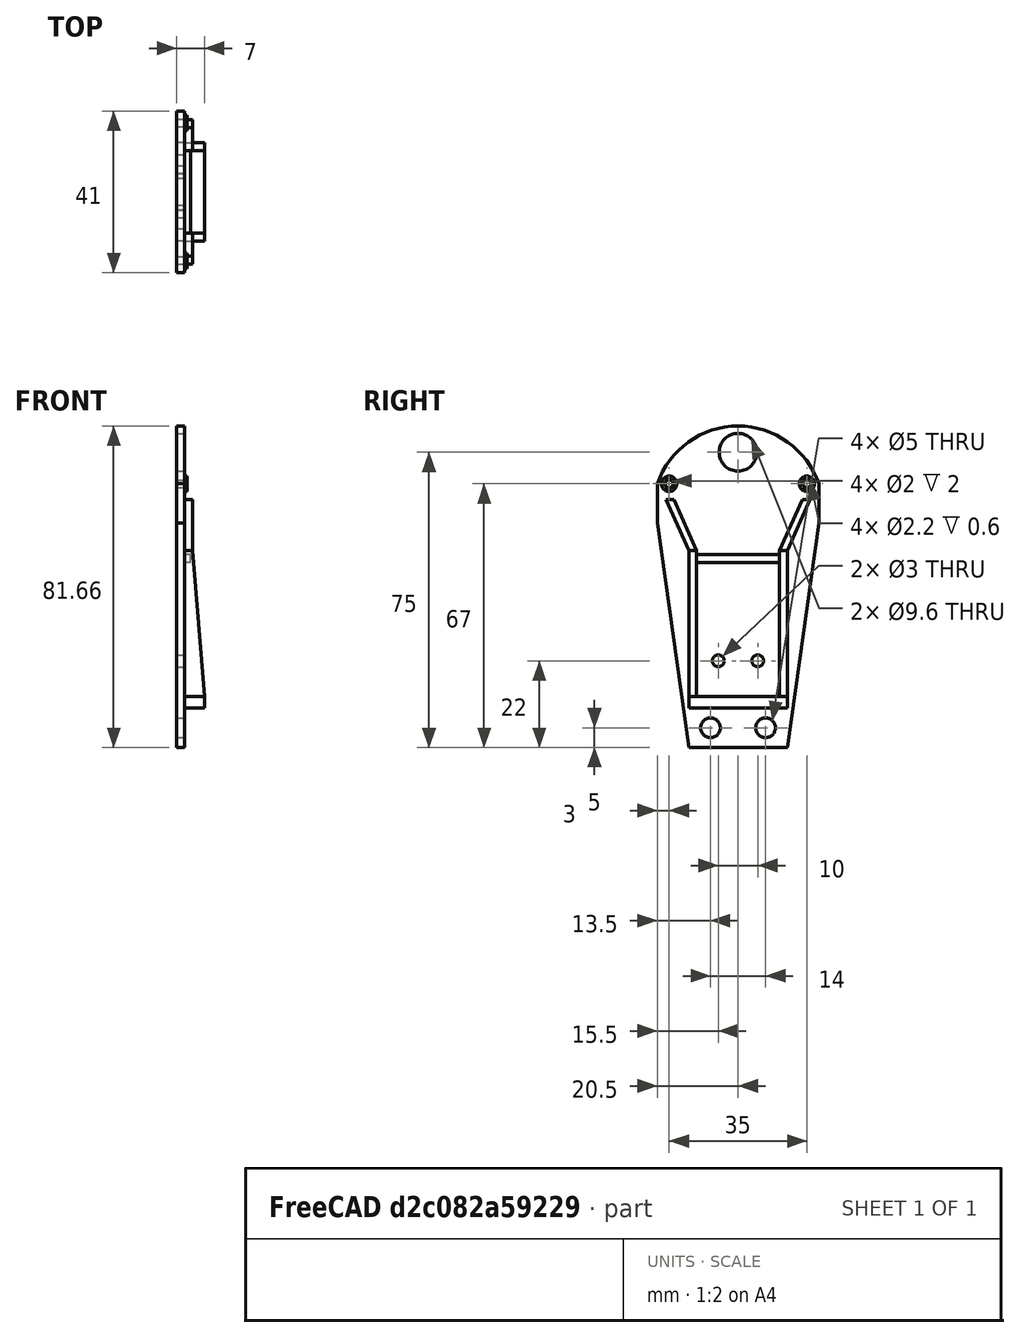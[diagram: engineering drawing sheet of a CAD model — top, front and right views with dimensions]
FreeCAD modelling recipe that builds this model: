
FCSTD DOCUMENT  (FreeCAD 0.16R4740 (Git))
Label: backplane
License: CC-BY 3.0
LicenseURL: http://creativecommons.org/licenses/by/3.0/
objects: Sketcher::SketchObject×6, Part::Fuse×6, PartDesign::Pad×5, Part::Mirroring×2, Part::MultiFuse×1, Part::Box×1, PartDesign::Pocket×1, Mesh::Feature×1
note: 28 computed .brp shape members not serialized (recipe doc carries the construction recipe); baked Part::Feature solids carry a one-line shape summary decoded from their .brp

FEATURE [Sketcher::SketchObject] Sketch001
  Placement = pos=(0,0,0) rot=(0.57735,-0.57735,-0.57735;2.0944rad)
  sketch-geometry (11):
    g0: Circle CenterX=0 CenterY=8 CenterZ=0 NormalX=0 NormalY=0 NormalZ=1 Radius=4.8
    g1: Circle CenterX=-17.5 CenterY=0 CenterZ=0 NormalX=0 NormalY=0 NormalZ=1 Radius=1
    g2: Circle CenterX=17.5 CenterY=0 CenterZ=0 NormalX=0 NormalY=0 NormalZ=1 Radius=1
    g3: ArcOfCircle CenterX=0 CenterY=-7 CenterZ=0 NormalX=0 NormalY=0 NormalZ=1 Radius=21.6622 StartAngle=0.32905 EndAngle=2.81254
    g4: LineSegment StartX=-20.5 StartY=0 StartZ=0 EndX=-20.5 EndY=-10 EndZ=0
    g5: LineSegment StartX=-20.5 StartY=-10 StartZ=0 EndX=-12.5 EndY=-67 EndZ=0
    g6: LineSegment StartX=-12.5 StartY=-67 StartZ=0 EndX=12.5 EndY=-67 EndZ=0
    g7: LineSegment StartX=12.5 StartY=-67 StartZ=0 EndX=20.5 EndY=-10 EndZ=0
    g8: LineSegment StartX=20.5 StartY=-10 StartZ=0 EndX=20.5 EndY=0 EndZ=0
    g9: Circle CenterX=-7 CenterY=-62 CenterZ=0 NormalX=0 NormalY=0 NormalZ=1 Radius=2.5
    g10: Circle CenterX=7 CenterY=-62 CenterZ=0 NormalX=0 NormalY=0 NormalZ=1 Radius=2.5
  constraints (34):
    c: Radius(g0) = 4.8
    c: DistanceY(g-1,g0) = 8
    c: DistanceX(g-1,g0) = 0
    c: DistanceX(g2,g1) = -35
    c: Radius(g1) = 1
    c: Radius(g2) = 1
    c: DistanceX(g-1,g1) = -17.5
    c: DistanceY(g1,g2) = 0
    c: DistanceY(g-1,g1) = 0
    c: DistanceX(g-1,g3) = 0
    c: DistanceY(g3,g3) = 0
    c: Coincident(g4,g5)
    c: Coincident(g5,g6)
    c: Horizontal(g6)
    c: Coincident(g6,g7)
    c: Coincident(g7,g8)
    c: Coincident(g8,g3)
    c: Vertical(g4)
    c: Vertical(g8)
    c: Coincident(g3,g4)
    c: DistanceX(g6) = 25
    c: DistanceX(g-1,g5) = -12.5
    c: Equal(g4,g8)
    c: DistanceY(g3,g1) = 0
    c: DistanceX(g3,g1) = 3
    c: Distance(g4) = 10
    c: DistanceY(g-1,g3) = -7
    c: Radius(g9) = 2.5
    c: Radius(g10) = 2.5
    c: DistanceY(g9,g10) = 0
    c: DistanceX(g9) = -7
    c: DistanceY(g5,g9) = 5
    c: DistanceY(g6,g0) = 75
    c: DistanceX(g9,g10) = 14
FEATURE [Sketcher::SketchObject] Sketch
  Placement = pos=(0,0,0) rot=(-0.57735,0.57735,-0.57735;2.0944rad)
  sketch-geometry (4):
    g0: Circle CenterX=-17.5 CenterY=0 CenterZ=0 NormalX=0 NormalY=0 NormalZ=1 Radius=1.1
    g1: Circle CenterX=-17.5 CenterY=0 CenterZ=0 NormalX=0 NormalY=0 NormalZ=1 Radius=1.95
    g2: Circle CenterX=17.5 CenterY=0 CenterZ=0 NormalX=0 NormalY=0 NormalZ=1 Radius=1.1
    g3: Circle CenterX=17.5 CenterY=0 CenterZ=0 NormalX=0 NormalY=0 NormalZ=1 Radius=1.95
  constraints (6):
    c: Radius(g0) = 1.1
    c: Coincident(g1,g0)
    c: Radius(g1) = 1.95
    c: Radius(g2) = 1.1
    c: Coincident(g2,g3)
    c: Radius(g3) = 1.95
FEATURE [PartDesign::Pad] Pad
  Length = 2
  Length2 = 100
  Placement = pos=(0,0,0) rot=(0.57735,-0.57735,-0.57735;2.0944rad)
  Sketch = -> Sketch001
  Type = 0
FEATURE [PartDesign::Pad] Pad001
  Length = 0.6
  Length2 = 100
  Placement = pos=(0,0,0) rot=(-0.57735,0.57735,-0.57735;2.0944rad)
  Sketch = -> Sketch
  Type = 0
FEATURE [Part::MultiFuse] Fusion
  Shapes = -> [Pad001,Pad]
FEATURE [Sketcher::SketchObject] Sketch006
  Placement = pos=(0,0,0) rot=(0.57735,0.57735,0.57735;2.0944rad)
  sketch-geometry (4):
    g0: LineSegment StartX=-12.5 StartY=-54 StartZ=0 EndX=12.5 EndY=-54 EndZ=0
    g1: LineSegment StartX=12.5 StartY=-54 StartZ=0 EndX=12.5 EndY=-57 EndZ=0
    g2: LineSegment StartX=12.5 StartY=-57 StartZ=0 EndX=-12.5 EndY=-57 EndZ=0
    g3: LineSegment StartX=-12.5 StartY=-57 StartZ=0 EndX=-12.5 EndY=-54 EndZ=0
  constraints (12):
    c: Coincident(g0,g1)
    c: Coincident(g1,g2)
    c: Coincident(g2,g3)
    c: Coincident(g3,g0)
    c: Horizontal(g0)
    c: Horizontal(g2)
    c: Vertical(g1)
    c: Vertical(g3)
    c: Symmetric(g0,g0,g-2)
    c: Distance(g1) = 3
    c: Distance(g2) = 25
    c: DistanceY(g-1,g2) = -57
FEATURE [Sketcher::SketchObject] Sketch007
  Placement = pos=(0,-12.5,0) rot=(-0.57735,-0.57735,0.57735;4.18879rad)
  sketch-geometry (4):
    g0: LineSegment StartX=53.9987 StartY=0 StartZ=0 EndX=53.9987 EndY=5 EndZ=0
    g1: LineSegment StartX=53.9987 StartY=0 StartZ=0 EndX=16.9987 EndY=0 EndZ=0
    g2: LineSegment StartX=16.9987 StartY=0 StartZ=0 EndX=16.9987 EndY=2 EndZ=0
    g3: LineSegment StartX=16.9987 StartY=2 StartZ=0 EndX=53.9987 EndY=5 EndZ=0
  constraints (11):
    c: Coincident(g1,g0)
    c: PointOnObject(g1,g-1)
    c: Coincident(g2,g1)
    c: Vertical(g2)
    c: Coincident(g3,g2)
    c: Coincident(g3,g0)
    c: Distance(g1,g0) = 37
    c: Distance(g1,g2) = 2
    c: Vertical(g0)
    c: Distance(g0,g0) = 5
    c: Horizontal(g1)
FEATURE [Sketcher::SketchObject] Sketch008
  Placement = pos=(0,0,0) rot=(0.57735,0.57735,0.57735;2.0944rad)
  sketch-geometry (4):
    g0: LineSegment StartX=-12.5 StartY=-17 StartZ=0 EndX=-18.3156 EndY=-4 EndZ=0
    g1: LineSegment StartX=-18.3156 StartY=-4 StartZ=0 EndX=-16.3156 EndY=-4 EndZ=0
    g2: LineSegment StartX=-16.3156 StartY=-4 StartZ=0 EndX=-10.5 EndY=-17 EndZ=0
    g3: LineSegment StartX=-10.5 StartY=-17 StartZ=0 EndX=-12.5 EndY=-17 EndZ=0
  constraints (11):
    c: Coincident(g1,g0)
    c: Horizontal(g1)
    c: Coincident(g2,g1)
    c: Coincident(g3,g2)
    c: Coincident(g3,g0)
    c: Parallel(g0,g2)
    c: Horizontal(g3)
    c: Distance(g3) = 2
    c: DistanceX(g-1,g0) = -12.5
    c: DistanceY(g-1,g2) = -17
    c: DistanceY(g-1,g1) = -4
FEATURE [PartDesign::Pad] Pad003
  Length = 2
  Length2 = 100
  Placement = pos=(0,0,0) rot=(0.57735,0.57735,0.57735;2.0944rad)
  Sketch = -> Sketch008
  Type = 0
FEATURE [PartDesign::Pad] Pad004
  Length = 2
  Length2 = 100
  Placement = pos=(0,-12.5,0) rot=(-0.57735,-0.57735,0.57735;4.18879rad)
  Reversed = true
  Sketch = -> Sketch007
  Type = 0
FEATURE [PartDesign::Pad] Pad005
  Length = 5
  Length2 = 100
  Placement = pos=(0,0,0) rot=(0.57735,0.57735,0.57735;2.0944rad)
  Sketch = -> Sketch006
  Type = 0
FEATURE [Part::Mirroring] Part__Mirroring  label="Pad003 (Mirror #1)"
  Base = (0,0,0)
  Normal = (0,1,0)
  Source = -> Pad003
FEATURE [Part::Mirroring] Part__Mirroring001  label="Pad004 (Mirror #2)"
  Base = (0,0,0)
  Normal = (0,1,0)
  Source = -> Pad004
FEATURE [Part::Box] Box  label="Cube"
  Height = 2
  Length = 1.5
  Placement = pos=(0,-12.5,-20) rot=(0,0,1;0rad)
  Width = 25
FEATURE [Sketcher::SketchObject] Sketch009
  Placement = pos=(0,0,0) rot=(0.57735,0.57735,0.57735;2.0944rad)
  Support = -> Fusion [Face4]
  sketch-geometry (2):
    g0: Circle CenterX=-5 CenterY=-45 CenterZ=0 NormalX=0 NormalY=0 NormalZ=1 Radius=1.5
    g1: Circle CenterX=5 CenterY=-45 CenterZ=0 NormalX=0 NormalY=0 NormalZ=1 Radius=1.5
  constraints (5):
    c: Symmetric(g0,g1,g-2)
    c: Radius(g0) = 1.5
    c: Radius(g1) = 1.5
    c: DistanceX(g-1,g1) = 5
    c: DistanceY(g-1,g1) = -45
FEATURE [PartDesign::Pocket] Pocket
  Length = 5
  Sketch = -> Sketch009
  Type = 0
FEATURE [Part::Fuse] Fusion001
  Base = -> Pad003
  Tool = -> Pad004
FEATURE [Part::Fuse] Fusion002
  Base = -> Part__Mirroring
  Tool = -> Part__Mirroring001
FEATURE [Part::Fuse] Fusion003
  Base = -> Pad005
  Tool = -> Box
FEATURE [Part::Fuse] Fusion004
  Base = -> Fusion001
  Tool = -> Fusion002
FEATURE [Part::Fuse] Fusion005
  Base = -> Fusion003
  Tool = -> Fusion004
FEATURE [Part::Fuse] Fusion006
  Base = -> Pocket
  Tool = -> Fusion005
FEATURE [Mesh::Feature] Mesh  label="Fusion006 (Meshed)"
